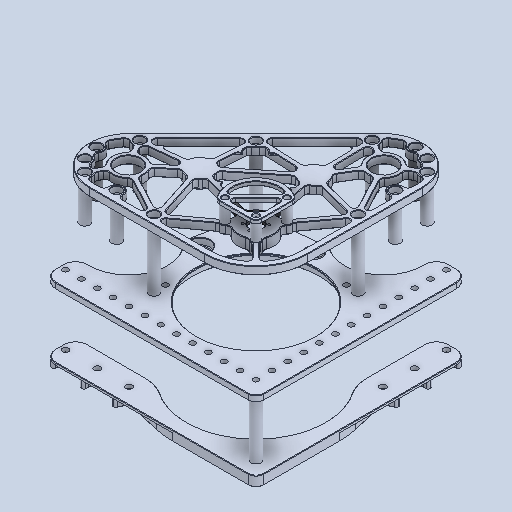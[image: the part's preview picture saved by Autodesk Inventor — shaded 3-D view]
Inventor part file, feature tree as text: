
AUTODESK INVENTOR PART (.ipt)
format: ipt  version: 2024.2 (Build 282272000, 272)  size: 1,548,800 bytes
history: native  units: in
note: dims shown in document units (in); Inventor stores cm internally (conversion verified against a paired STEP export)
features: other x15, chamfer x4
ambient origin geometry x8: Origin, YZ Plane, XZ Plane, XY Plane, X Axis, Y Axis, Z Axis, Center Point
bodies: Solid1 (feature_tree), Solid2 (feature_tree), Solid3 (feature_tree), Solid4 (feature_tree), Solid5 (feature_tree), Solid6 (feature_tree), Solid7 (feature_tree), Solid8 (feature_tree), Solid9 (feature_tree), Solid10 (feature_tree), Solid11 (feature_tree), Solid12 (feature_tree), Solid13 (feature_tree), Solid14 (feature_tree), Solid15 (feature_tree), Solid16 (feature_tree), Solid17 (feature_tree), Solid18 (feature_tree), Solid19 (feature_tree)
feature tree (19):
  other  "Boss-Extrude4[1]"
  other  "Boss-Extrude4[2]"
  other  "Boss-Extrude4[3]"
  other  "Boss-Extrude6[1]"
  other  "Boss-Extrude6[2]"
  other  "Boss-Extrude6[3]"
  other  "Boss-Extrude6[4]"
  other  "Boss-Extrude6[5]"
  other  "Boss-Extrude6[6]"
  other  "Boss-Extrude6[7]"
  other  "Boss-Extrude6[8]"
  other  "Boss-Extrude9[1]"
  other  "Boss-Extrude17[1]"
  other  "Boss-Extrude17[2]"
  other  "Boss-Extrude17[3]"
  chamfer  "Chamfer4"  [1 undecoded]
  chamfer  "Chamfer1"  [1 undecoded]
  chamfer  "Chamfer3"  [1 undecoded]
  chamfer  "Chamfer2"  [1 undecoded]
note: 4 required parameter values undecoded (feature->parameter linkage not recoverable at this tier; creation-order binding heuristic only, values carry confidence <= 0.55)
